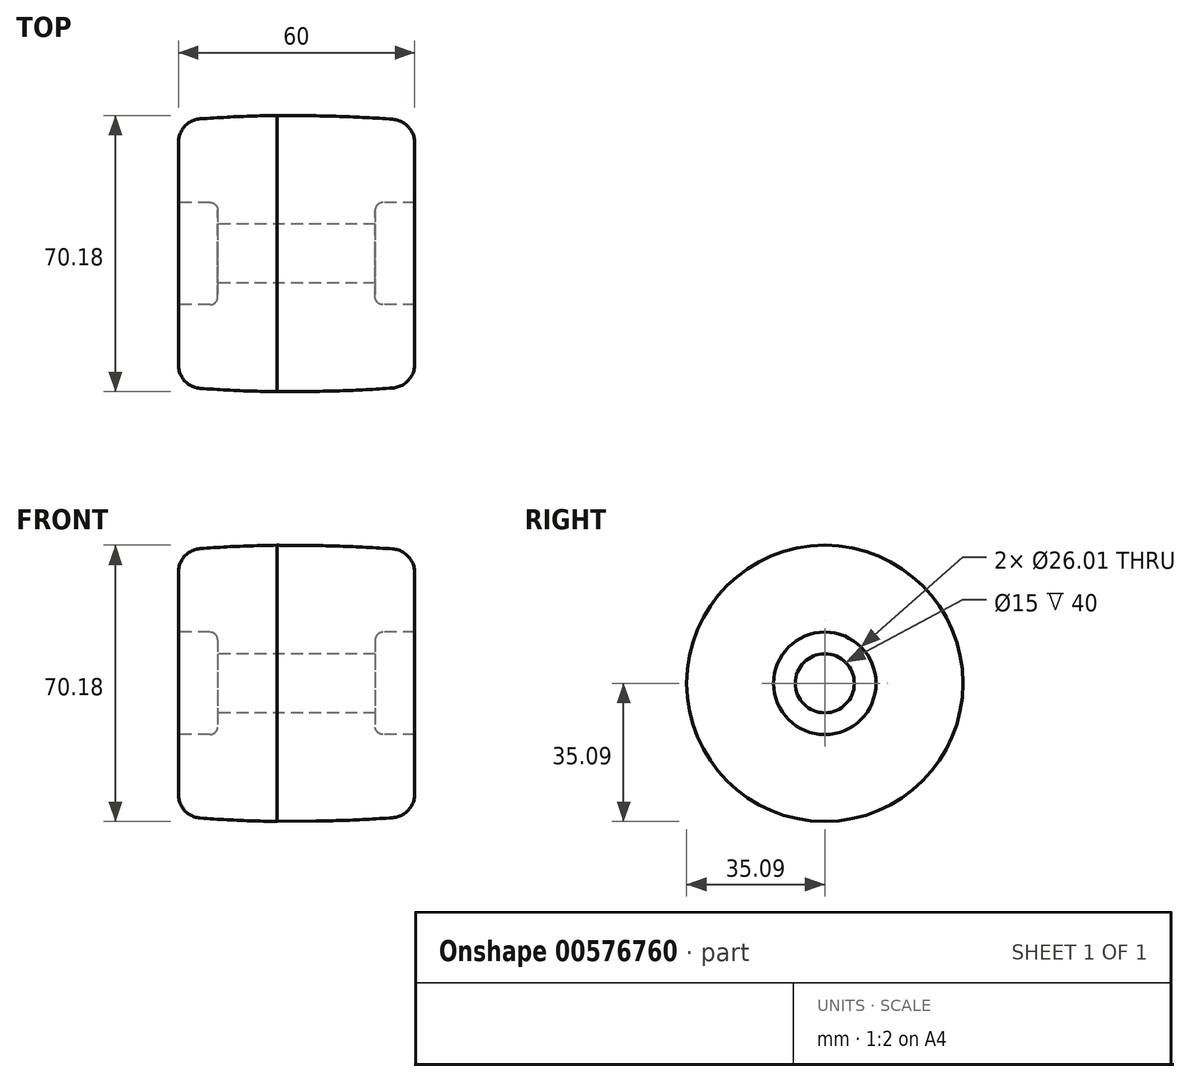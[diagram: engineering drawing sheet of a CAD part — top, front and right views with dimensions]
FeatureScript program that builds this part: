
annotation { "Feature Type Name" : "Feature", "Feature Type Description" : "" }
export const myFeature = defineFeature(function(context is Context, id is Id, definition is map)
    precondition{}
    {
        {
            var Q0;
            Q0=qCreatedBy(makeId("Front.planeOp"),FACE);
            var sketch = newSketch(context, id + "F0", { "sketchPlane" : qUnion([Q0])});
            skLineSegment(sketch, "E0", {"start": v(-56.97, 0) * mm, "end": v(61.31, 0) * mm, "construction": true});
            skLineSegment(sketch, "E1", {"start": v(0, 0) * mm, "end": v(0, -300) * mm});
            skPoint(sketch, "E2.startSnap0", {"position": v(-5, 35.1) * mm});
            skArc(sketch, "E3", {"start": v(-5, 35.1) * mm, "mid": v(-14.72, 34.8) * mm, "end": v(-24.44, 34.24) * mm});
            skArc(sketch, "E4", {"start": v(5, 35) * mm, "mid": v(14.73, 34.71) * mm, "end": v(24.44, 34.14) * mm});
            skLineSegment(sketch, "E5", {"start": v(-5, 35.1) * mm, "end": v(5, 35) * mm});
            skPoint(sketch, "E6.visualSharp", {"position": v(30, 33.7) * mm});
            skArc(sketch, "E6.filletArc", {"start": v(30, 28.16) * mm, "mid": v(28.4, 32.25) * mm, "end": v(24.44, 34.14) * mm});
            skPoint(sketch, "E7.visualSharp", {"position": v(-30, 33.78) * mm});
            skArc(sketch, "E7.filletArc", {"start": v(-24.44, 34.24) * mm, "mid": v(-28.4, 32.34) * mm, "end": v(-30, 28.25) * mm});
            skLineSegment(sketch, "E8", {"start": v(-20, 7.5) * mm, "end": v(20, 7.5) * mm});
            skLineSegment(sketch, "E9", {"start": v(20, 7.5) * mm, "end": v(20, 11) * mm});
            skLineSegment(sketch, "E10", {"start": v(22, 13) * mm, "end": v(30, 13) * mm});
            skLineSegment(sketch, "E11", {"start": v(30, 13) * mm, "end": v(30, 28.16) * mm});
            skLineSegment(sketch, "E12", {"start": v(-20, 7.5) * mm, "end": v(-20, 11) * mm});
            skLineSegment(sketch, "E13", {"start": v(-22, 13) * mm, "end": v(-30, 13) * mm});
            skLineSegment(sketch, "E14", {"start": v(-30, 13) * mm, "end": v(-30, 28.25) * mm});
            skPoint(sketch, "E15.visualSharp", {"position": v(20, 13) * mm});
            skArc(sketch, "E15.filletArc", {"start": v(22, 13) * mm, "mid": v(20.59, 12.42) * mm, "end": v(20, 11) * mm});
            skPoint(sketch, "E16.visualSharp", {"position": v(-20, 13) * mm});
            skArc(sketch, "E16.filletArc", {"start": v(-20, 11) * mm, "mid": v(-20.59, 12.42) * mm, "end": v(-22, 13) * mm});
            skSolve(sketch);
        }
        {
            var Q0;
            Q0=makeQuery(id+"F0.imprint","IMPRINT",FACE,{"disambiguationData":[TD([[makeQuery(id+"F0.imprint","IMPRINT",EDGE,{"derivedFrom":sQuery(id+"F0.wireOp",EDGE,"E3")}),1.0]])]});
            var Q1;
            Q1=sQuery(id+"F0.wireOp",EDGE,"E0");
            revolve(context, id + "F1", {"entities" : qUnion([Q0]), "axis" : qUnion([Q1]), "revolveType" : RevolveType.FULL});
        }
    });
